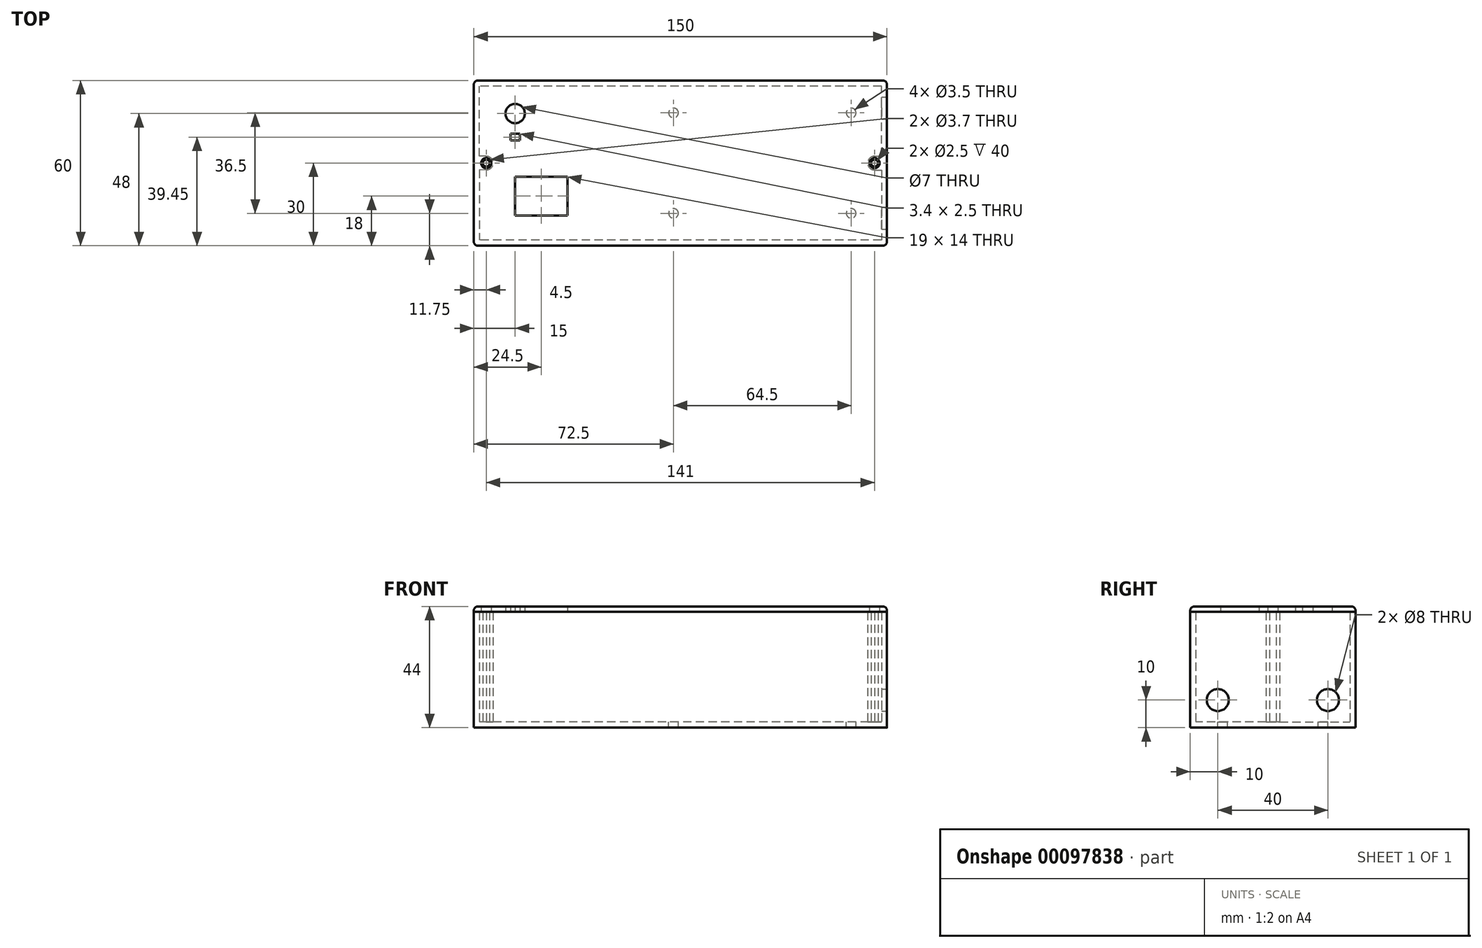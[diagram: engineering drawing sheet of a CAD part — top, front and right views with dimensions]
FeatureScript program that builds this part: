
annotation { "Feature Type Name" : "Feature", "Feature Type Description" : "" }
export const myFeature = defineFeature(function(context is Context, id is Id, definition is map)
    precondition{}
    {
        {
            var Q0;
            Q0=qCreatedBy(makeId("Top.planeOp"),FACE);
            var sketch = newSketch(context, id + "F0", { "sketchPlane" : qUnion([Q0])});
            skLineSegment(sketch, "E0.bottom", {"start": v(75, 30) * mm, "end": v(-75, 30) * mm});
            skLineSegment(sketch, "E0.top", {"start": v(75, -30) * mm, "end": v(-75, -30) * mm});
            skLineSegment(sketch, "E0.left", {"start": v(75, 30) * mm, "end": v(75, -30) * mm});
            skLineSegment(sketch, "E0.right", {"start": v(-75, 30) * mm, "end": v(-75, -30) * mm});
            skPoint(sketch, "E0.middle", {"position": v(0, 0) * mm});
            skCircle(sketch, "E1", {"center": v(62, 18.25) * mm, "radius": 1.75 * mm});
            skCircle(sketch, "E2", {"center": v(62, -18.25) * mm, "radius": 1.75 * mm});
            skCircle(sketch, "E3", {"center": v(-2.5, 18.25) * mm, "radius": 1.75 * mm});
            skCircle(sketch, "E4", {"center": v(-2.5, -18.25) * mm, "radius": 1.75 * mm});
            skSolve(sketch);
        }
        {
            var Q0;
            Q0=makeQuery(id+"F0.imprint","IMPRINT",FACE,{"disambiguationData":[TD([[makeQuery(id+"F0.imprint","IMPRINT",EDGE,{"derivedFrom":sQuery(id+"F0.wireOp",EDGE,"E0.bottom")}),1.0]])]});
            extrude(context, id + "F1", {"entities" : qUnion([Q0]), "oppositeDirection" : true, "depth" : 2 * mm});
        }
        {
            var Q0;
            Q0=qCreatedBy(makeId("Top.planeOp"),FACE);
            var sketch = newSketch(context, id + "F2", { "sketchPlane" : qUnion([Q0])});
            skLineSegment(sketch, "E5.bottom", {"start": v(75, 30) * mm, "end": v(-75, 30) * mm});
            skLineSegment(sketch, "E5.top", {"start": v(-75, -30) * mm, "end": v(75, -30) * mm});
            skLineSegment(sketch, "E5.left", {"start": v(-75, -30) * mm, "end": v(-75, 30) * mm});
            skLineSegment(sketch, "E5.right", {"start": v(75, -30) * mm, "end": v(75, 30) * mm});
            skPoint(sketch, "E5.middle", {"position": v(0, 0) * mm});
            skLineSegment(sketch, "E6.bottom", {"start": v(73, 28) * mm, "end": v(-73, 28) * mm});
            skLineSegment(sketch, "E6.top", {"start": v(73, -28) * mm, "end": v(-73, -28) * mm});
            skLineSegment(sketch, "E6.left", {"start": v(-73, 2.5) * mm, "end": v(-73, 28) * mm});
            skLineSegment(sketch, "E6.right", {"start": v(73, 2.48) * mm, "end": v(73, 28) * mm});
            skArc(sketch, "E7", {"start": v(-70.55, -2.5) * mm, "mid": v(-68, 0) * mm, "end": v(-70.57, 2.5) * mm});
            skCircle(sketch, "E8", {"center": v(-70.5, 0) * mm, "radius": 1.25 * mm});
            skLineSegment(sketch, "E9", {"start": v(-70.43, 2.5) * mm, "end": v(-73, 2.5) * mm});
            skLineSegment(sketch, "E10", {"start": v(-70.55, -2.5) * mm, "end": v(-73, -2.45) * mm});
            skArc(sketch, "E11", {"start": v(70.52, 2.5) * mm, "mid": v(68, 0) * mm, "end": v(70.54, -2.5) * mm});
            skCircle(sketch, "E12", {"center": v(70.5, 0) * mm, "radius": 1.25 * mm});
            skLineSegment(sketch, "E13", {"start": v(70.52, 2.5) * mm, "end": v(73, 2.48) * mm});
            skLineSegment(sketch, "E14", {"start": v(70.54, -2.5) * mm, "end": v(73, -2.5) * mm});
            skLineSegment(sketch, "E15.trimOffspring", {"start": v(73, -2.5) * mm, "end": v(73, -28) * mm});
            skLineSegment(sketch, "E16.trimOffspring", {"start": v(-73, -2.45) * mm, "end": v(-73, -28) * mm});
            skSolve(sketch);
        }
        {
            var Q0;
            {var subQ1=sQuery(id+"F2.wireOp",EDGE,"E5.bottom");Q0=makeQuery(id+"F2.imprint","IMPRINT",FACE,{"disambiguationData":[TD([[makeQuery(id+"F2.imprint","IMPRINT",EDGE,{"derivedFrom":subQ1}),-1.0]])]});}
            var Q1;
            Q1=makeQuery(id+"F2.imprint","IMPRINT",FACE,{"disambiguationData":[TD([[makeQuery(id+"F2.imprint","IMPRINT",EDGE,{"derivedFrom":sQuery(id+"F2.wireOp",EDGE,"E8")}),-1.0]])]});
            var Q2;
            Q2=makeQuery(id+"F2.imprint","IMPRINT",FACE,{"disambiguationData":[TD([[makeQuery(id+"F2.imprint","IMPRINT",EDGE,{"derivedFrom":sQuery(id+"F2.wireOp",EDGE,"E11")}),1.0]])]});
            extrude(context, id + "F3", {"entities" : qUnion([Q0, Q1, Q2]), "operationType" : NewBodyOperationType.ADD, "depth" : 40 * mm});
        }
        {
            var Q0;
            Q0=makeQuery(id+"F3.opExtrude","CAP_FACE",FACE,{"disambiguationData":[OSD([sQuery(id+"F2.wireOp",EDGE,"E5.bottom"),sQuery(id+"F2.wireOp",EDGE,"E5.top"),sQuery(id+"F2.wireOp",EDGE,"E5.left"),sQuery(id+"F2.wireOp",EDGE,"E5.right"),sQuery(id+"F2.wireOp",EDGE,"E6.bottom"),sQuery(id+"F2.wireOp",EDGE,"E6.top"),sQuery(id+"F2.wireOp",EDGE,"E6.left"),sQuery(id+"F2.wireOp",EDGE,"E6.right"),sQuery(id+"F2.wireOp",EDGE,"E7"),sQuery(id+"F2.wireOp",EDGE,"E8"),sQuery(id+"F2.wireOp",EDGE,"E9"),sQuery(id+"F2.wireOp",EDGE,"E10"),sQuery(id+"F2.wireOp",EDGE,"E11"),sQuery(id+"F2.wireOp",EDGE,"E12"),sQuery(id+"F2.wireOp",EDGE,"E13"),sQuery(id+"F2.wireOp",EDGE,"E14"),sQuery(id+"F2.wireOp",EDGE,"E15.trimOffspring"),sQuery(id+"F2.wireOp",EDGE,"E16.trimOffspring")])],"isStart":false});
            var sketch = newSketch(context, id + "F4", { "sketchPlane" : qUnion([Q0])});
            skLineSegment(sketch, "E17.bottom", {"start": v(-75, 30) * mm, "end": v(75, 30) * mm});
            skLineSegment(sketch, "E17.top", {"start": v(-75, -30) * mm, "end": v(75, -30) * mm});
            skLineSegment(sketch, "E17.left", {"start": v(-75, 30) * mm, "end": v(-75, -30) * mm});
            skLineSegment(sketch, "E17.right", {"start": v(75, 30) * mm, "end": v(75, -30) * mm});
            skPoint(sketch, "E17.middle", {"position": v(0, 0) * mm});
            skCircle(sketch, "E18", {"center": v(-60, 18) * mm, "radius": 3.5 * mm});
            skLineSegment(sketch, "E19.bottom", {"start": v(-61.7, 10.7) * mm, "end": v(-58.3, 10.7) * mm});
            skLineSegment(sketch, "E19.top", {"start": v(-61.7, 8.2) * mm, "end": v(-58.3, 8.2) * mm});
            skLineSegment(sketch, "E19.left", {"start": v(-61.7, 10.7) * mm, "end": v(-61.7, 8.2) * mm});
            skLineSegment(sketch, "E19.right", {"start": v(-58.3, 10.7) * mm, "end": v(-58.3, 8.2) * mm});
            skLineSegment(sketch, "E20", {"start": v(-60, 18) * mm, "end": v(-60, -12.7) * mm, "construction": true});
            skLineSegment(sketch, "E21.bottom", {"start": v(-60, -5) * mm, "end": v(-41, -5) * mm});
            skLineSegment(sketch, "E21.top", {"start": v(-60, -19) * mm, "end": v(-41, -19) * mm});
            skLineSegment(sketch, "E21.left", {"start": v(-60, -5) * mm, "end": v(-60, -19) * mm});
            skLineSegment(sketch, "E21.right", {"start": v(-41, -5) * mm, "end": v(-41, -19) * mm});
            skCircle(sketch, "E22", {"center": v(-70.5, 0) * mm, "radius": 1.85 * mm});
            skCircle(sketch, "E23", {"center": v(70.5, 0) * mm, "radius": 1.85 * mm});
            skSolve(sketch);
        }
        {
            var Q0;
            Q0=makeQuery(id+"F4.imprint","IMPRINT",FACE,{"disambiguationData":[TD([[makeQuery(id+"F4.imprint","IMPRINT",EDGE,{"derivedFrom":sQuery(id+"F4.wireOp",EDGE,"E18")}),-1.0]])]});
            var Q1;
            Q1=makeQuery(id+"F4.imprint","IMPRINT",FACE,{"disambiguationData":[TD([[makeQuery(id+"F4.imprint","IMPRINT",EDGE,{"derivedFrom":sQuery(id+"F4.wireOp",EDGE,"E17.bottom")}),1.0]])]});
            extrude(context, id + "F5", {"entities" : qUnion([Q0, Q1]), "depth" : 2 * mm});
        }
        {
            var Q0;
            Q0=makeQuery(id+"F5.opExtrude","CAP_EDGE",EDGE,{"disambiguationData":[OSD([sQuery(id+"F4.wireOp",EDGE,"E17.right")])],"isStart":false});
            var Q1;
            Q1=makeQuery(id+"F5.opExtrude","CAP_EDGE",EDGE,{"disambiguationData":[OSD([sQuery(id+"F4.wireOp",EDGE,"E17.bottom")])],"isStart":false});
            var Q2;
            Q2=makeQuery(id+"F5.opExtrude","CAP_EDGE",EDGE,{"disambiguationData":[OSD([sQuery(id+"F4.wireOp",EDGE,"E17.top")])],"isStart":false});
            var Q3;
            Q3=makeQuery(id+"F5.opExtrude","CAP_EDGE",EDGE,{"disambiguationData":[OSD([sQuery(id+"F4.wireOp",EDGE,"E17.left")])],"isStart":false});
            var Q4;
            Q4=makeQuery(id+"F5.opExtrude","SWEPT_EDGE",EDGE,{"disambiguationData":[OSD([sQuery(id+"F4.wireOp",EDGE,"E17.bottom"),sQuery(id+"F4.wireOp",EDGE,"E17.right")])]});
            var Q5;
            Q5=makeQuery(id+"F5.opExtrude","SWEPT_EDGE",EDGE,{"disambiguationData":[OSD([sQuery(id+"F4.wireOp",EDGE,"E17.top"),sQuery(id+"F4.wireOp",EDGE,"E17.right")])]});
            var Q6;
            Q6=makeQuery(id+"F5.opExtrude","SWEPT_EDGE",EDGE,{"disambiguationData":[OSD([sQuery(id+"F4.wireOp",EDGE,"E17.top"),sQuery(id+"F4.wireOp",EDGE,"E17.left")])]});
            var Q7;
            Q7=makeQuery(id+"F5.opExtrude","SWEPT_EDGE",EDGE,{"disambiguationData":[OSD([sQuery(id+"F4.wireOp",EDGE,"E17.bottom"),sQuery(id+"F4.wireOp",EDGE,"E17.left")])]});
            fillet(context, id + "F6", {"entities" : qUnion([Q0, Q1, Q2, Q3, Q4, Q5, Q6, Q7]), "radius" : 1.5 * mm, "tangentPropagation" : true, "allowEdgeOverflow" : false});
        }
        {
            var Q0;
            Q0=makeQuery(id+"F3.boolean.opBoolean","MERGE",EDGE,{"derivedFrom":[makeQuery(id+"F1.opExtrude","SWEPT_EDGE",EDGE,{"disambiguationData":[OSD([sQuery(id+"F0.wireOp",EDGE,"E0.top"),sQuery(id+"F0.wireOp",EDGE,"E0.right")])]}),makeQuery(id+"F3.opExtrude","SWEPT_EDGE",EDGE,{"disambiguationData":[OSD([sQuery(id+"F2.wireOp",EDGE,"E5.top"),sQuery(id+"F2.wireOp",EDGE,"E5.left")])]})]});
            var Q1;
            Q1=makeQuery(id+"F3.boolean.opBoolean","MERGE",EDGE,{"derivedFrom":[makeQuery(id+"F1.opExtrude","SWEPT_EDGE",EDGE,{"disambiguationData":[OSD([sQuery(id+"F0.wireOp",EDGE,"E0.bottom"),sQuery(id+"F0.wireOp",EDGE,"E0.right")])]}),makeQuery(id+"F3.opExtrude","SWEPT_EDGE",EDGE,{"disambiguationData":[OSD([sQuery(id+"F2.wireOp",EDGE,"E5.bottom"),sQuery(id+"F2.wireOp",EDGE,"E5.left")])]})]});
            var Q2;
            Q2=makeQuery(id+"F3.boolean.opBoolean","MERGE",EDGE,{"derivedFrom":[makeQuery(id+"F1.opExtrude","SWEPT_EDGE",EDGE,{"disambiguationData":[OSD([sQuery(id+"F0.wireOp",EDGE,"E0.top"),sQuery(id+"F0.wireOp",EDGE,"E0.left")])]}),makeQuery(id+"F3.opExtrude","SWEPT_EDGE",EDGE,{"disambiguationData":[OSD([sQuery(id+"F2.wireOp",EDGE,"E5.top"),sQuery(id+"F2.wireOp",EDGE,"E5.right")])]})]});
            var Q3;
            Q3=makeQuery(id+"F3.boolean.opBoolean","MERGE",EDGE,{"derivedFrom":[makeQuery(id+"F1.opExtrude","SWEPT_EDGE",EDGE,{"disambiguationData":[OSD([sQuery(id+"F0.wireOp",EDGE,"E0.bottom"),sQuery(id+"F0.wireOp",EDGE,"E0.left")])]}),makeQuery(id+"F3.opExtrude","SWEPT_EDGE",EDGE,{"disambiguationData":[OSD([sQuery(id+"F2.wireOp",EDGE,"E5.bottom"),sQuery(id+"F2.wireOp",EDGE,"E5.right")])]})]});
            fillet(context, id + "F7", {"entities" : qUnion([Q0, Q1, Q2, Q3]), "radius" : 1.5 * mm, "tangentPropagation" : true, "allowEdgeOverflow" : false});
        }
        {
            var Q0;
            Q0=makeQuery(id+"F3.boolean.opBoolean","MERGE",FACE,{"derivedFrom":[makeQuery(id+"F1.opExtrude","SWEPT_FACE",FACE,{"disambiguationData":[OSD([sQuery(id+"F0.wireOp",EDGE,"E0.left")])]}),makeQuery(id+"F3.opExtrude","SWEPT_FACE",FACE,{"disambiguationData":[OSD([sQuery(id+"F2.wireOp",EDGE,"E5.right")])]})]});
            var sketch = newSketch(context, id + "F8", { "sketchPlane" : qUnion([Q0])});
            skCircle(sketch, "E24", {"center": v(-20, 8) * mm, "radius": 4 * mm});
            skCircle(sketch, "E25", {"center": v(20, 8) * mm, "radius": 4 * mm});
            skSolve(sketch);
        }
        {
            var Q0;
            Q0=makeQuery(id+"F8.imprint","IMPRINT",FACE,{"disambiguationData":[TD([[makeQuery(id+"F8.imprint","IMPRINT",EDGE,{"derivedFrom":sQuery(id+"F8.wireOp",EDGE,"E24")}),1.0]])]});
            var Q1;
            Q1=makeQuery(id+"F8.imprint","IMPRINT",FACE,{"disambiguationData":[TD([[makeQuery(id+"F8.imprint","IMPRINT",EDGE,{"derivedFrom":sQuery(id+"F8.wireOp",EDGE,"E25")}),1.0]])]});
            extrude(context, id + "F9", {"entities" : qUnion([Q0, Q1]), "operationType" : NewBodyOperationType.REMOVE, "oppositeDirection" : true, "depth" : 3 * mm});
        }
    });
